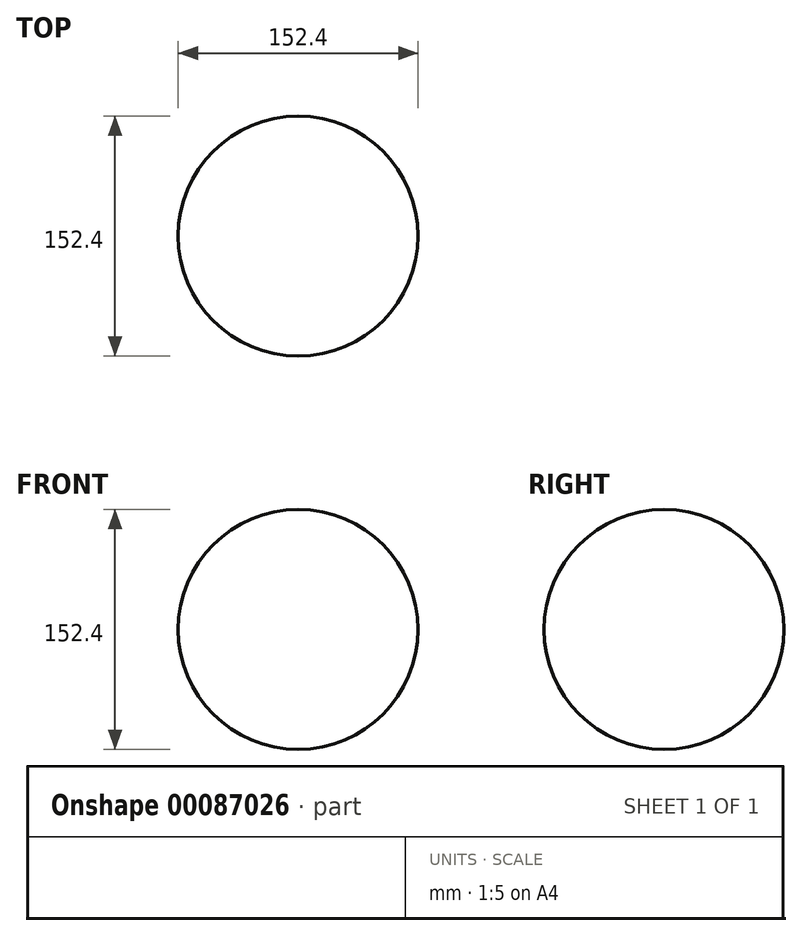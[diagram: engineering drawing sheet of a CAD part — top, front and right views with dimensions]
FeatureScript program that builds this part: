
annotation { "Feature Type Name" : "Feature", "Feature Type Description" : "" }
export const myFeature = defineFeature(function(context is Context, id is Id, definition is map)
    precondition{}
    {
        {
            var Q0;
            Q0=qCreatedBy(makeId("Top.planeOp"),FACE);
            var sketch = newSketch(context, id + "F0", { "sketchPlane" : qUnion([Q0])});
            skCircle(sketch, "E0", {"center": v(0, 0) * mm, "radius": 76.2 * mm});
            skSolve(sketch);
        }
        {
            var Q0;
            Q0=makeQuery(id+"F0.imprint","IMPRINT",FACE,{"disambiguationData":[TD([[makeQuery(id+"F0.imprint","IMPRINT",EDGE,{"derivedFrom":sQuery(id+"F0.wireOp",EDGE,"E0")}),1.0]])]});
            extrude(context, id + "F1", {"entities" : qUnion([Q0]), "endBound" : BoundingType.SYMMETRIC, "depth" : 152.4 * mm});
        }
        {
            var Q0;
            Q0=makeQuery(id+"F1.opExtrude","CAP_EDGE",EDGE,{"disambiguationData":[OSD([sQuery(id+"F0.wireOp",EDGE,"E0")])],"isStart":false});
            var Q1;
            Q1=makeQuery(id+"F1.opExtrude","CAP_EDGE",EDGE,{"disambiguationData":[OSD([sQuery(id+"F0.wireOp",EDGE,"E0")])],"isStart":true});
            fillet(context, id + "F2", {"entities" : qUnion([Q0, Q1]), "radius" : 76.2 * mm, "tangentPropagation" : true, "allowEdgeOverflow" : false});
        }
    });
